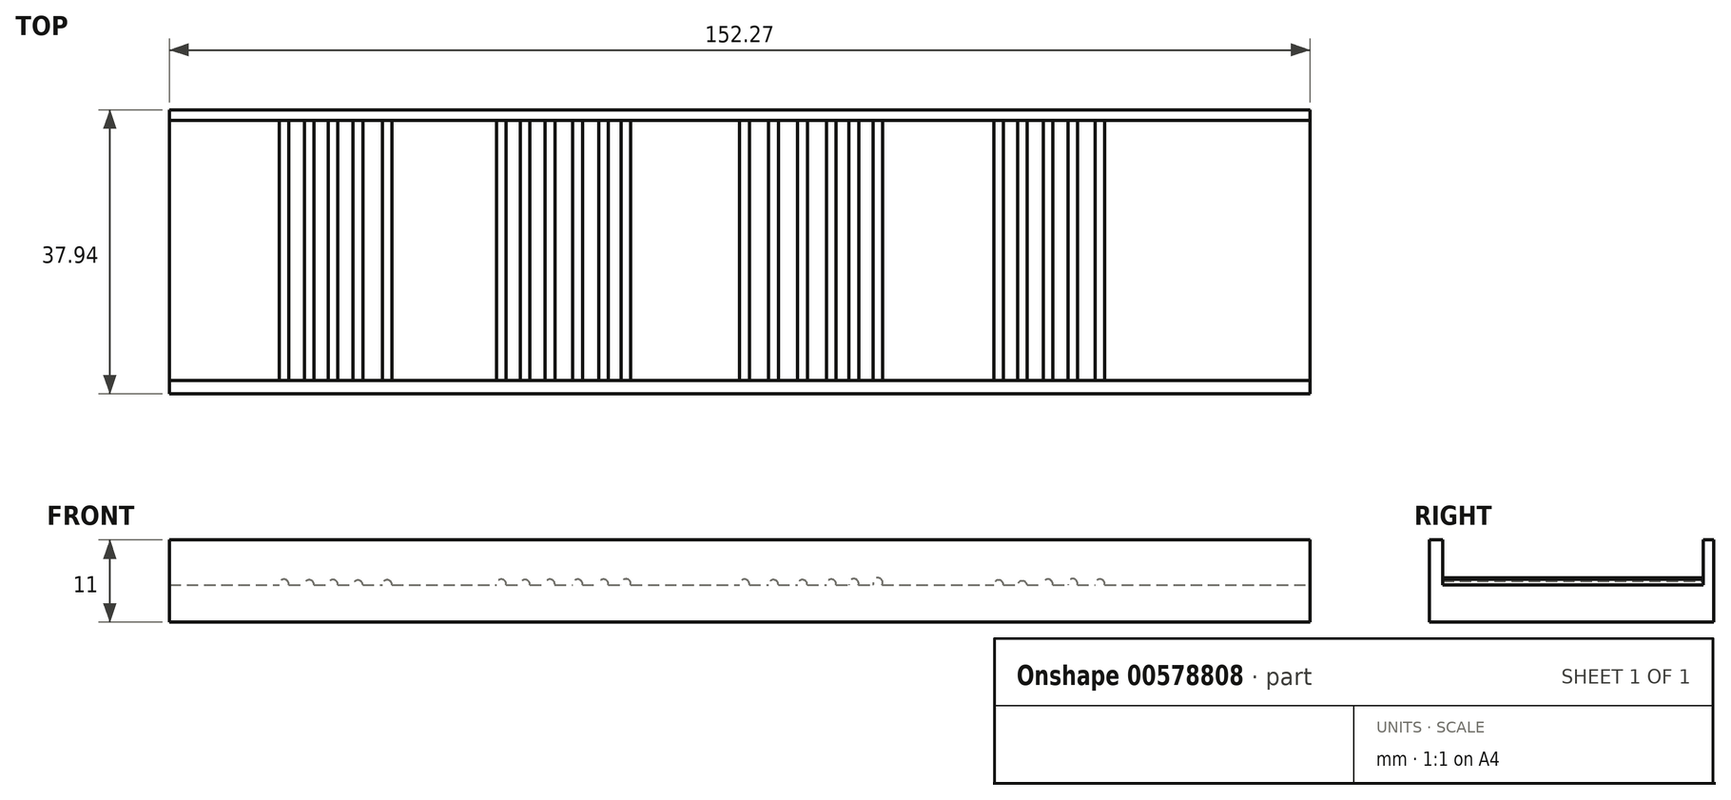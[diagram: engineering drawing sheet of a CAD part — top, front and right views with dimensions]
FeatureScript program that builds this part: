
annotation { "Feature Type Name" : "Feature", "Feature Type Description" : "" }
export const myFeature = defineFeature(function(context is Context, id is Id, definition is map)
    precondition{}
    {
        {
            var Q0;
            Q0=qCreatedBy(makeId("Top.planeOp"),FACE);
            var sketch = newSketch(context, id + "F0", { "sketchPlane" : qUnion([Q0])});
            skLineSegment(sketch, "E0.bottom", {"start": v(-75.14, 0) * mm, "end": v(77.13, 0) * mm});
            skLineSegment(sketch, "E0.top", {"start": v(-75.14, -37.94) * mm, "end": v(77.13, -37.94) * mm});
            skLineSegment(sketch, "E0.left", {"start": v(-75.14, 0) * mm, "end": v(-75.14, -37.94) * mm});
            skLineSegment(sketch, "E0.right", {"start": v(77.13, 0) * mm, "end": v(77.13, -37.94) * mm});
            skSolve(sketch);
        }
        {
            var Q0;
            Q0 = qSketchRegion(id + "F0", true);
            extrude(context, id + "F1", {"entities" : qUnion([Q0]), "depth" : 5 * mm, "offsetDistance" : 25 * mm});
        }
        {
            var Q0;
            Q0=makeQuery(id+"F1.opExtrude","CAP_FACE",FACE,{"disambiguationData":[OSD([sQuery(id+"F0.wireOp",EDGE,"E0.bottom"),sQuery(id+"F0.wireOp",EDGE,"E0.top"),sQuery(id+"F0.wireOp",EDGE,"E0.left"),sQuery(id+"F0.wireOp",EDGE,"E0.right")])],"isStart":false});
            var sketch = newSketch(context, id + "F2", { "sketchPlane" : qUnion([Q0])});
            skLineSegment(sketch, "E1.bottom", {"start": v(-75.14, 0) * mm, "end": v(77.13, 0) * mm});
            skLineSegment(sketch, "E1.top", {"start": v(-75.14, -1.4) * mm, "end": v(77.13, -1.4) * mm});
            skLineSegment(sketch, "E1.left", {"start": v(-75.14, 0) * mm, "end": v(-75.14, -1.4) * mm});
            skLineSegment(sketch, "E1.right", {"start": v(77.13, 0) * mm, "end": v(77.13, -1.4) * mm});
            skLineSegment(sketch, "E2.bottom", {"start": v(-75.14, -37.94) * mm, "end": v(77.13, -37.94) * mm});
            skLineSegment(sketch, "E2.top", {"start": v(-75.14, -37.94) * mm, "end": v(77.13, -37.94) * mm});
            skLineSegment(sketch, "E2.left", {"start": v(-75.14, -37.94) * mm, "end": v(-75.14, -37.94) * mm});
            skLineSegment(sketch, "E2.right", {"start": v(77.13, -37.94) * mm, "end": v(77.13, -37.94) * mm});
            skLineSegment(sketch, "E3.top", {"start": v(-75.14, -36.18) * mm, "end": v(77.13, -36.18) * mm});
            skLineSegment(sketch, "E3.left", {"start": v(-75.14, -37.94) * mm, "end": v(-75.14, -36.18) * mm});
            skLineSegment(sketch, "E3.right", {"start": v(77.13, -37.94) * mm, "end": v(77.13, -36.18) * mm});
            skSolve(sketch);
        }
        {
            var Q0;
            Q0=qCreatedBy(makeId("Front.planeOp"),FACE);
            var sketch = newSketch(context, id + "F3", { "sketchPlane" : qUnion([Q0])});
            skLineSegment(sketch, "E4.bottom", {"start": v(-67.36, 5.09) * mm, "end": v(-64.85, 5.09) * mm});
            skLineSegment(sketch, "E4.top", {"start": v(-67.36, 6) * mm, "end": v(-64.85, 6) * mm});
            skLineSegment(sketch, "E4.left", {"start": v(-67.36, 5.09) * mm, "end": v(-67.36, 6) * mm});
            skLineSegment(sketch, "E4.right", {"start": v(-64.85, 5.09) * mm, "end": v(-64.85, 6) * mm});
            skLineSegment(sketch, "E5.bottom", {"start": v(-37.18, 5.2) * mm, "end": v(-34.6, 5.2) * mm});
            skLineSegment(sketch, "E5.top", {"start": v(-37.18, 6.07) * mm, "end": v(-34.6, 6.07) * mm});
            skLineSegment(sketch, "E5.left", {"start": v(-34.6, 5.2) * mm, "end": v(-34.6, 6.07) * mm});
            skLineSegment(sketch, "E5.right", {"start": v(-37.18, 5.2) * mm, "end": v(-37.18, 6.07) * mm});
            skLineSegment(sketch, "E6.bottom", {"start": v(-5.98, 5.26) * mm, "end": v(-3.47, 5.26) * mm});
            skLineSegment(sketch, "E6.top", {"start": v(-5.98, 5.92) * mm, "end": v(-3.47, 5.92) * mm});
            skLineSegment(sketch, "E6.left", {"start": v(-5.98, 5.26) * mm, "end": v(-5.98, 5.92) * mm});
            skLineSegment(sketch, "E6.right", {"start": v(-3.47, 5.26) * mm, "end": v(-3.47, 5.92) * mm});
            skLineSegment(sketch, "E7.bottom", {"start": v(24.85, 5.17) * mm, "end": v(27.35, 5.17) * mm});
            skLineSegment(sketch, "E7.top", {"start": v(24.85, 6.08) * mm, "end": v(27.35, 6.08) * mm});
            skLineSegment(sketch, "E7.left", {"start": v(24.85, 5.17) * mm, "end": v(24.85, 6.08) * mm});
            skLineSegment(sketch, "E7.right", {"start": v(27.35, 5.17) * mm, "end": v(27.35, 6.08) * mm});
            skLineSegment(sketch, "E8.bottom", {"start": v(54.29, 5.43) * mm, "end": v(56.8, 5.43) * mm});
            skLineSegment(sketch, "E8.top", {"start": v(54.29, 6.34) * mm, "end": v(56.8, 6.34) * mm});
            skLineSegment(sketch, "E8.left", {"start": v(54.29, 5.43) * mm, "end": v(54.29, 6.34) * mm});
            skLineSegment(sketch, "E8.right", {"start": v(56.8, 5.43) * mm, "end": v(56.8, 6.34) * mm});
            skSolve(sketch);
        }
        {
            var Q0;
            Q0 = qConstructionFilter(qBodyType(qCreatedBy(id + "F3" ,EDGE), BodyType.WIRE), ConstructionObject.NO);
            extrude(context, id + "F4", {"bodyType" : ToolBodyType.SURFACE, "surfaceEntities" : qUnion([Q0]), "depth" : 38 * mm, "offsetDistance" : 25 * mm});
        }
        {
            var Q0;
            Q0=qCreatedBy(makeId("Front.planeOp"),FACE);
            var sketch = newSketch(context, id + "F5", { "sketchPlane" : qUnion([Q0])});
            skCircle(sketch, "E9", {"center": v(-59.89, 5.08) * mm, "radius": 0.65 * mm});
            skCircle(sketch, "E10", {"center": v(-56.51, 5) * mm, "radius": 0.65 * mm});
            skCircle(sketch, "E11", {"center": v(-46.1, 5) * mm, "radius": 0.65 * mm});
            skCircle(sketch, "E12", {"center": v(-50, 4.96) * mm, "radius": 0.65 * mm});
            skCircle(sketch, "E13", {"center": v(-53.33, 5.04) * mm, "radius": 0.65 * mm});
            skCircle(sketch, "E14", {"center": v(-30.85, 5.08) * mm, "radius": 0.65 * mm});
            skCircle(sketch, "E15", {"center": v(-14.2, 5.13) * mm, "radius": 0.65 * mm});
            skCircle(sketch, "E16", {"center": v(-17.19, 5.08) * mm, "radius": 0.65 * mm});
            skCircle(sketch, "E17", {"center": v(-20.65, 5.08) * mm, "radius": 0.65 * mm});
            skCircle(sketch, "E18", {"center": v(-24.35, 5.08) * mm, "radius": 0.65 * mm});
            skCircle(sketch, "E19", {"center": v(-27.67, 5.03) * mm, "radius": 0.65 * mm});
            skCircle(sketch, "E20", {"center": v(1.63, 5.08) * mm, "radius": 0.65 * mm});
            skCircle(sketch, "E21", {"center": v(19.43, 5.28) * mm, "radius": 0.65 * mm});
            skCircle(sketch, "E22", {"center": v(16.23, 5.15) * mm, "radius": 0.65 * mm});
            skCircle(sketch, "E23", {"center": v(13.23, 5.08) * mm, "radius": 0.65 * mm});
            skCircle(sketch, "E24", {"center": v(9.36, 5.02) * mm, "radius": 0.65 * mm});
            skCircle(sketch, "E25", {"center": v(5.5, 5.02) * mm, "radius": 0.65 * mm});
            skCircle(sketch, "E26", {"center": v(49.1, 5.1) * mm, "radius": 0.65 * mm});
            skCircle(sketch, "E27", {"center": v(45.46, 5.16) * mm, "radius": 0.65 * mm});
            skCircle(sketch, "E28", {"center": v(42.16, 5.09) * mm, "radius": 0.65 * mm});
            skCircle(sketch, "E29", {"center": v(38.73, 4.87) * mm, "radius": 0.65 * mm});
            skCircle(sketch, "E30", {"center": v(35.57, 4.98) * mm, "radius": 0.65 * mm});
            skSolve(sketch);
        }
        {
            var Q0;
            Q0 = qSketchRegion(id + "F5", true);
            extrude(context, id + "F6", {"entities" : qUnion([Q0]), "operationType" : NewBodyOperationType.ADD, "depth" : 37.9 * mm, "offsetDistance" : 25 * mm});
        }
        {
            var Q0;
            Q0 = qSketchRegion(id + "F2", true);
            extrude(context, id + "F7", {"entities" : qUnion([Q0]), "operationType" : NewBodyOperationType.ADD, "depth" : 6 * mm, "offsetDistance" : 25 * mm});
        }
    });
